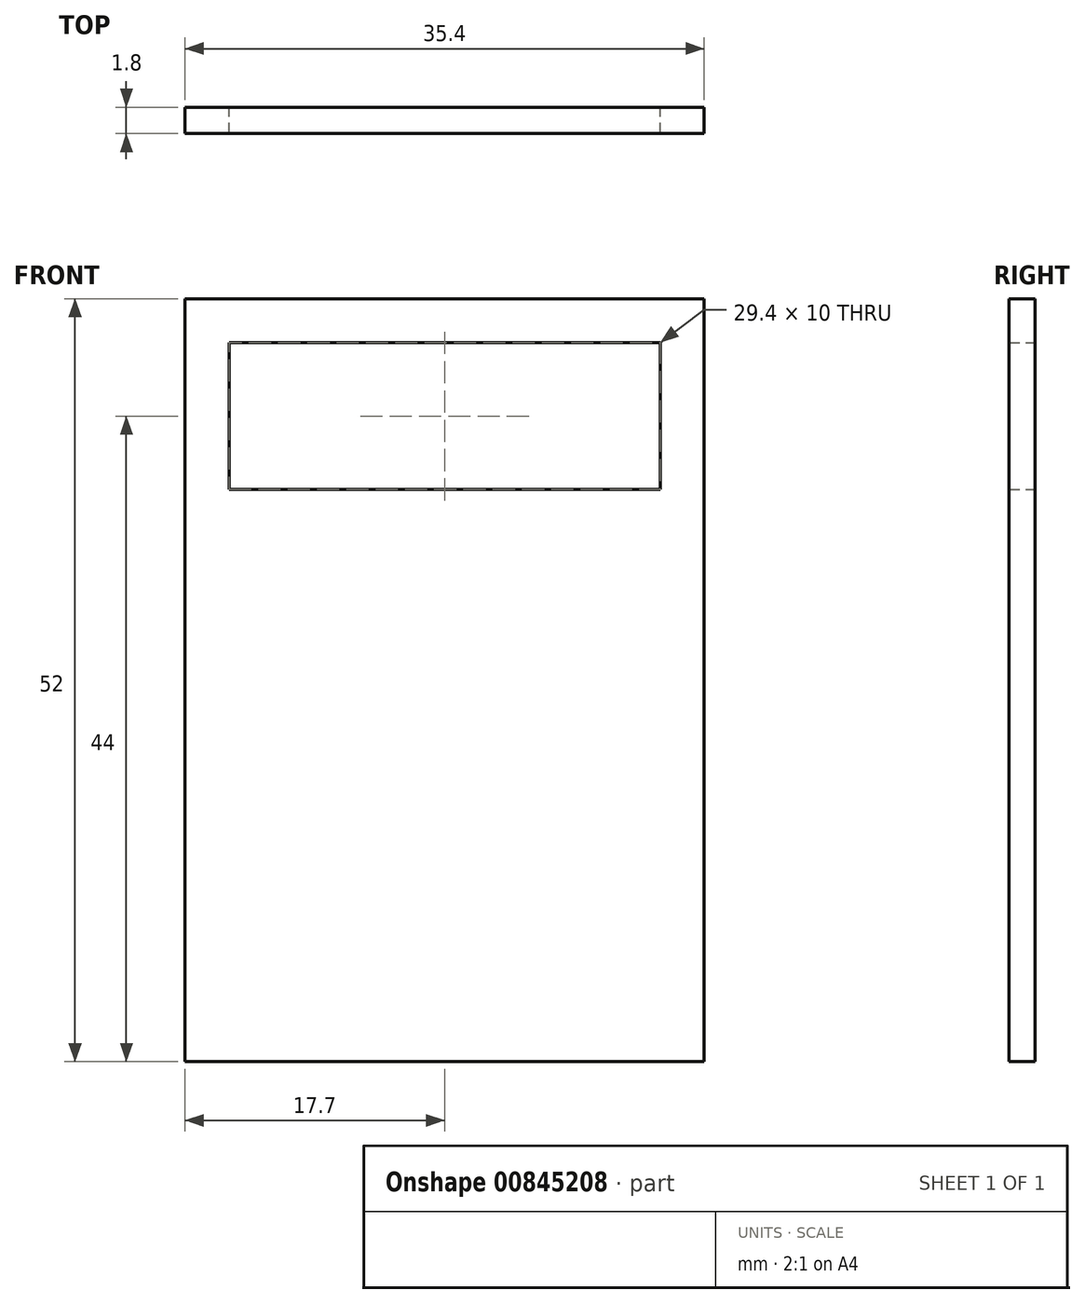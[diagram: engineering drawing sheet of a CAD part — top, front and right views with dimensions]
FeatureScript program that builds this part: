
annotation { "Feature Type Name" : "Feature", "Feature Type Description" : "" }
export const myFeature = defineFeature(function(context is Context, id is Id, definition is map)
    precondition{}
    {
        {
            var Q0;
            Q0=qCreatedBy(makeId("Front.planeOp"),FACE);
            var sketch = newSketch(context, id + "F0", { "sketchPlane" : qUnion([Q0])});
            skLineSegment(sketch, "E0.bottom", {"start": v(-17.7, 26) * mm, "end": v(17.7, 26) * mm});
            skLineSegment(sketch, "E0.top", {"start": v(-17.7, -26) * mm, "end": v(17.7, -26) * mm});
            skLineSegment(sketch, "E0.left", {"start": v(-17.7, 26) * mm, "end": v(-17.7, -26) * mm});
            skLineSegment(sketch, "E0.right", {"start": v(17.7, 26) * mm, "end": v(17.7, -26) * mm});
            skPoint(sketch, "E0.middle", {"position": v(0, 0) * mm});
            skLineSegment(sketch, "E1.bottom", {"start": v(-14.7, 13) * mm, "end": v(14.7, 13) * mm});
            skLineSegment(sketch, "E1.top", {"start": v(-14.7, 23) * mm, "end": v(14.7, 23) * mm});
            skLineSegment(sketch, "E1.left", {"start": v(-14.7, 13) * mm, "end": v(-14.7, 23) * mm});
            skLineSegment(sketch, "E1.right", {"start": v(14.7, 13) * mm, "end": v(14.7, 23) * mm});
            skPoint(sketch, "E1.middle", {"position": v(0, 18) * mm});
            skSolve(sketch);
        }
        {
            var Q0;
            Q0=qSketchRegion(id+"F0",true);
            extrude(context, id + "F1", {"entities" : qUnion([Q0]), "depth" : 1.8 * mm, "offsetDistance" : 25 * mm});
        }
    });
